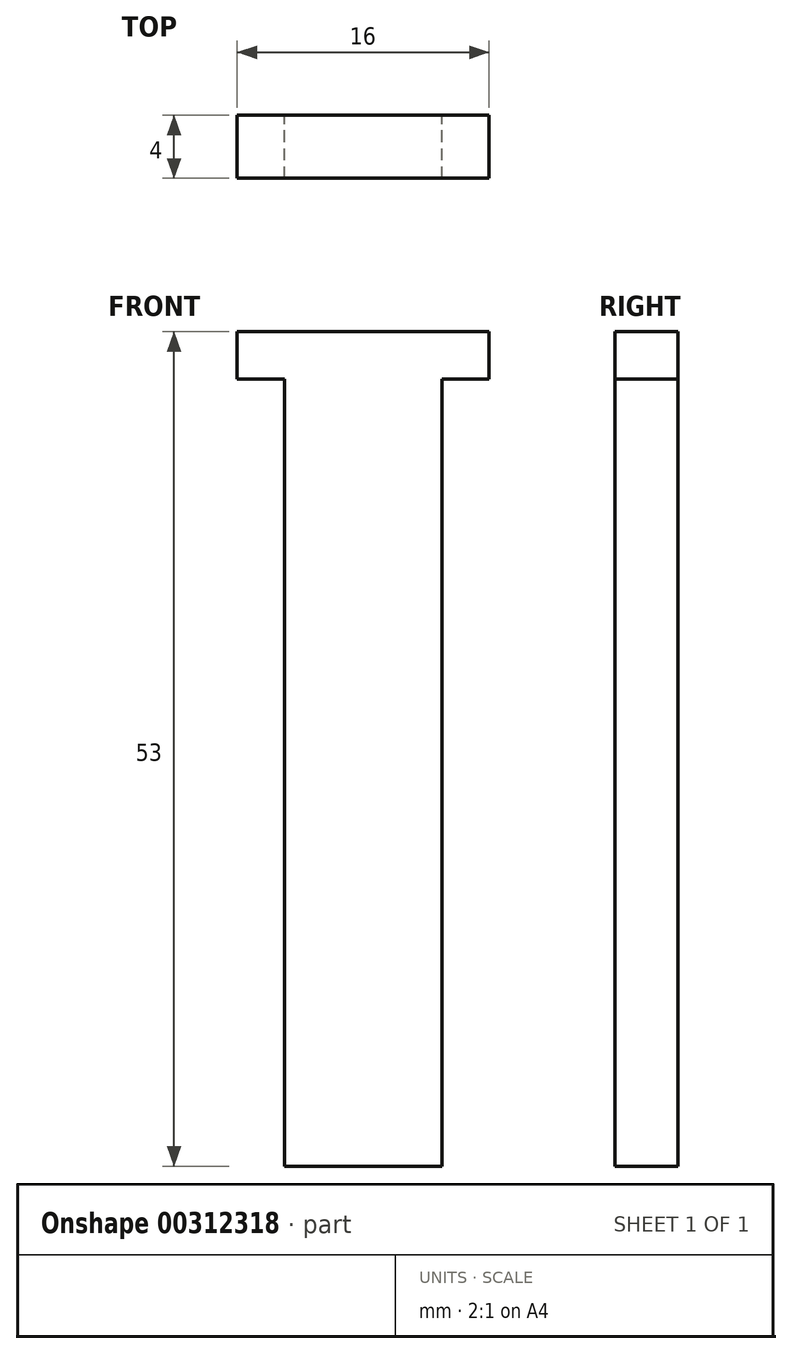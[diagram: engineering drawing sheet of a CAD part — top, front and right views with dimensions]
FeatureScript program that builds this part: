
annotation { "Feature Type Name" : "Feature", "Feature Type Description" : "" }
export const myFeature = defineFeature(function(context is Context, id is Id, definition is map)
    precondition{}
    {
        {
            var Q0;
            Q0=qCreatedBy(makeId("Front.planeOp"),FACE);
            var sketch = newSketch(context, id + "F0", { "sketchPlane" : qUnion([Q0])});
            skLineSegment(sketch, "E0", {"start": v(0, 0) * mm, "end": v(-5, 0) * mm});
            skLineSegment(sketch, "E1", {"start": v(-5, 0) * mm, "end": v(-5, 50) * mm});
            skLineSegment(sketch, "E2", {"start": v(-5, 50) * mm, "end": v(-8, 50) * mm});
            skLineSegment(sketch, "E3", {"start": v(-8, 50) * mm, "end": v(-8, 53) * mm});
            skLineSegment(sketch, "E4", {"start": v(-8, 53) * mm, "end": v(0, 53) * mm});
            skLineSegment(sketch, "E5", {"start": v(0, 53) * mm, "end": v(0, 0) * mm});
            skSolve(sketch);
        }
        {
            var Q0;
            Q0=makeQuery(id+"F0.imprint","IMPRINT",FACE,{"disambiguationData":[TD([[makeQuery(id+"F0.imprint","IMPRINT",EDGE,{"derivedFrom":sQuery(id+"F0.wireOp",EDGE,"E0")}),-1.0]])]});
            extrude(context, id + "F1", {"entities" : qUnion([Q0]), "depth" : 4 * mm});
        }
        {
            var Q0;
            Q0=makeQuery(id+"F1.opExtrude","SWEPT_BODY",BODY,{"disambiguationData":[OSD([sQuery(id+"F0.wireOp",EDGE,"E0"),sQuery(id+"F0.wireOp",EDGE,"E1"),sQuery(id+"F0.wireOp",EDGE,"E2"),sQuery(id+"F0.wireOp",EDGE,"E3"),sQuery(id+"F0.wireOp",EDGE,"E4"),sQuery(id+"F0.wireOp",EDGE,"E5")])]});
            var Q1;
            Q1=makeQuery(id+"F1.opExtrude","SWEPT_FACE",FACE,{"disambiguationData":[OSD([sQuery(id+"F0.wireOp",EDGE,"E5")])]});
            mirror(context, id + "F2", {"operationType" : NewBodyOperationType.ADD, "entities" : qUnion([Q0]), "mirrorPlane" : qUnion([Q1])});
        }
    });
